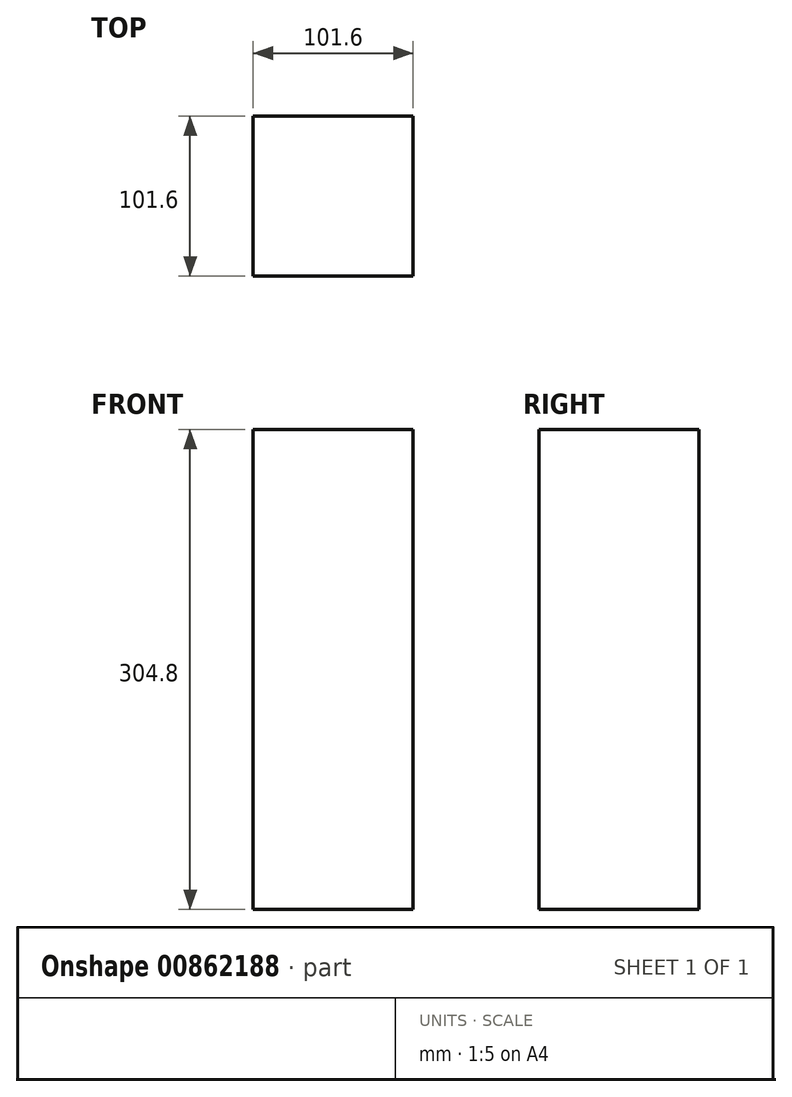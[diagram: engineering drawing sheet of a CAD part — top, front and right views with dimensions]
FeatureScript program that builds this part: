
annotation { "Feature Type Name" : "Feature", "Feature Type Description" : "" }
export const myFeature = defineFeature(function(context is Context, id is Id, definition is map)
    precondition{}
    {
        {
            var Q0;
            Q0=qCreatedBy(makeId("Top.planeOp"),FACE);
            var sketch = newSketch(context, id + "F0", { "sketchPlane" : qUnion([Q0])});
            skLineSegment(sketch, "E0.bottom", {"start": v(0, 0) * mm, "end": v(101.6, 0) * mm});
            skLineSegment(sketch, "E0.top", {"start": v(0, 101.6) * mm, "end": v(101.6, 101.6) * mm});
            skLineSegment(sketch, "E0.left", {"start": v(0, 0) * mm, "end": v(0, 101.6) * mm});
            skLineSegment(sketch, "E0.right", {"start": v(101.6, 0) * mm, "end": v(101.6, 101.6) * mm});
            skSolve(sketch);
        }
        {
            var Q0;
            Q0=makeQuery(id+"F0.imprint","IMPRINT",FACE,{"disambiguationData":[TD([[makeQuery(id+"F0.imprint","IMPRINT",EDGE,{"derivedFrom":sQuery(id+"F0.wireOp",EDGE,"E0.bottom")}),1.0]])]});
            extrude(context, id + "F1", {"entities" : qUnion([Q0]), "depth" : 304.8 * mm, "offsetDistance" : 25.4 * mm});
        }
    });
